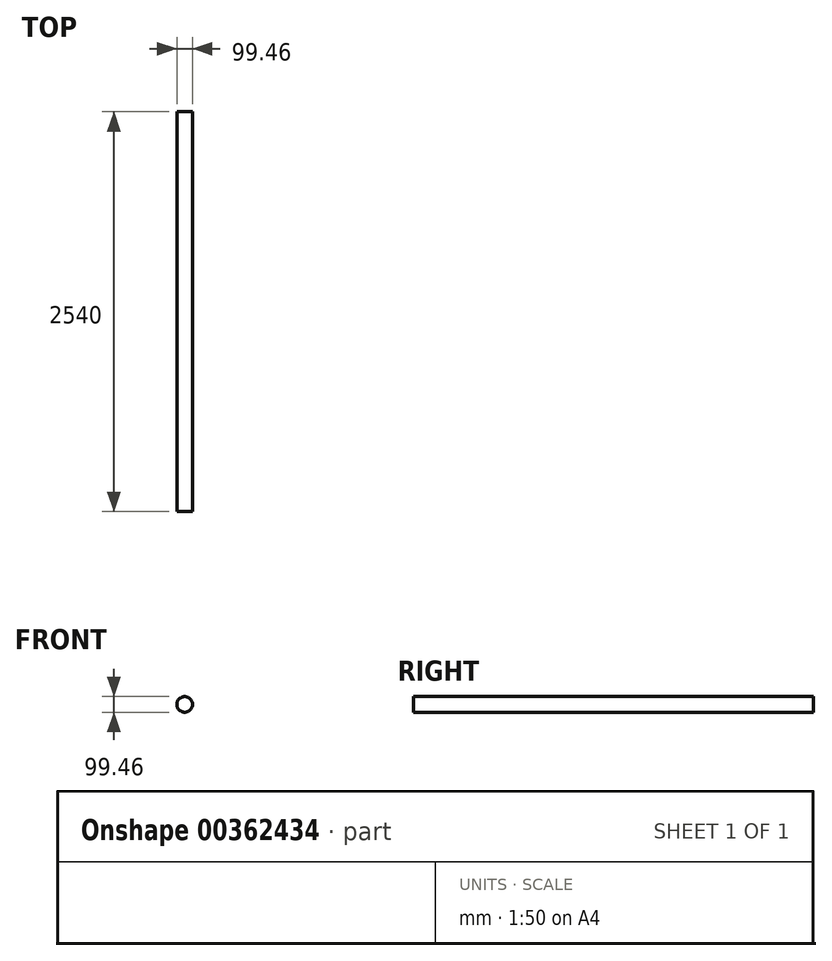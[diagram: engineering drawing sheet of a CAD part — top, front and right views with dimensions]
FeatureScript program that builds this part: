
annotation { "Feature Type Name" : "Feature", "Feature Type Description" : "" }
export const myFeature = defineFeature(function(context is Context, id is Id, definition is map)
    precondition{}
    {
        {
            var Q0;
            Q0=qCreatedBy(makeId("Front.planeOp"),FACE);
            var sketch = newSketch(context, id + "F0", { "sketchPlane" : qUnion([Q0])});
            skCircle(sketch, "E0", {"center": v(0, 0) * mm, "radius": 49.73 * mm});
            skSolve(sketch);
        }
        {
            var Q0;
            Q0=makeQuery(id+"F0.imprint","IMPRINT",FACE,{"disambiguationData":[TD([[makeQuery(id+"F0.imprint","IMPRINT",EDGE,{"derivedFrom":sQuery(id+"F0.wireOp",EDGE,"E0")}),1.0]])]});
            extrude(context, id + "F1", {"entities" : qUnion([Q0]), "depth" : 2540 * mm});
        }
    });
